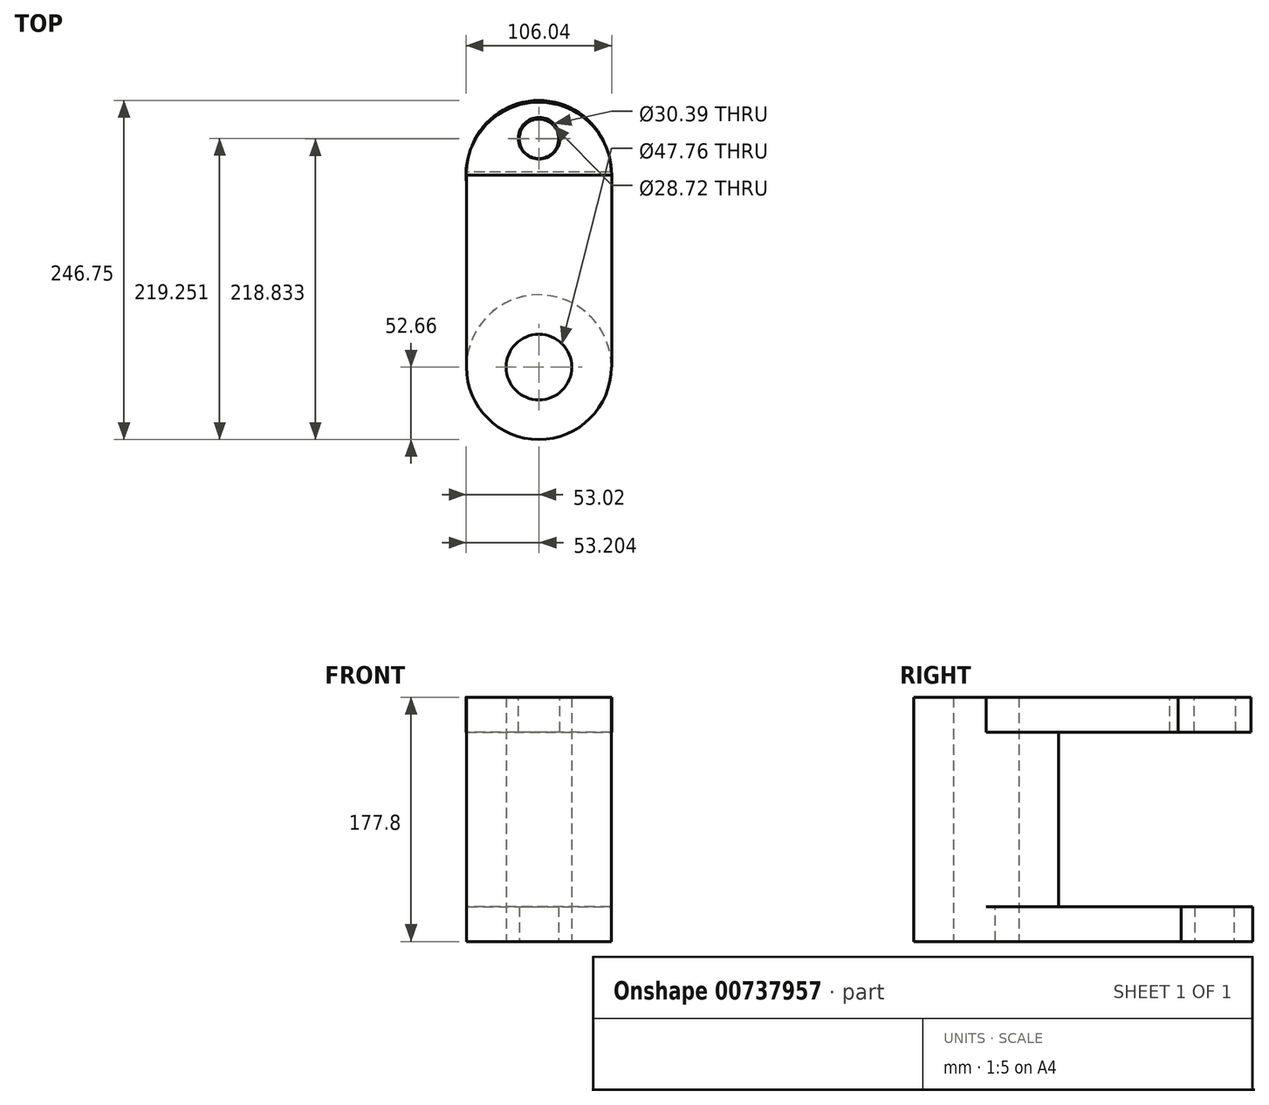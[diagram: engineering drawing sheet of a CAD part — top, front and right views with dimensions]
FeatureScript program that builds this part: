
annotation { "Feature Type Name" : "Feature", "Feature Type Description" : "" }
export const myFeature = defineFeature(function(context is Context, id is Id, definition is map)
    precondition{}
    {
        {
            var Q0;
            Q0=qCreatedBy(makeId("Top.planeOp"),FACE);
            var sketch = newSketch(context, id + "F0", { "sketchPlane" : qUnion([Q0])});
            skCircle(sketch, "E0", {"center": v(0, 0) * mm, "radius": 52.66 * mm});
            skCircle(sketch, "E1", {"center": v(0, 0) * mm, "radius": 23.88 * mm});
            skSolve(sketch);
        }
        {
            var Q0;
            Q0 = qSketchRegion(id + "F0", true);
            extrude(context, id + "F1", {"entities" : qUnion([Q0]), "depth" : 127 * mm, "offsetDistance" : 25.4 * mm});
        }
        {
            var Q0;
            Q0=makeQuery(id+"F1.opExtrude","CAP_FACE",FACE,{"disambiguationData":[OSD([sQuery(id+"F0.wireOp",EDGE,"E0"),sQuery(id+"F0.wireOp",EDGE,"E1")])],"isStart":false});
            var sketch = newSketch(context, id + "F2", { "sketchPlane" : qUnion([Q0])});
            skLineSegment(sketch, "E2.bottom", {"start": v(-52.66, 0) * mm, "end": v(53.02, 0) * mm});
            skLineSegment(sketch, "E2.top", {"start": v(-52.66, 76.3) * mm, "end": v(53.02, 76.3) * mm});
            skLineSegment(sketch, "E2.left", {"start": v(-52.66, 0) * mm, "end": v(-52.66, 76.3) * mm});
            skLineSegment(sketch, "E2.right", {"start": v(53.02, 0) * mm, "end": v(53.02, 76.3) * mm});
            skSolve(sketch);
        }
        {
            var Q0;
            {var subQ0=sQuery(id+"F2.wireOp",EDGE,"E2.bottom");var subQ1=makeQuery(id+"F1.opExtrude","CAP_EDGE",EDGE,{"disambiguationData":[OSD([sQuery(id+"F0.wireOp",EDGE,"E0")])],"isStart":false});var subQ6=makeQuery(id+"F2.imprint","INTERSECT",VERTEX,{"derivedFrom":[subQ1,subQ0]});Q0=makeQuery(id+"F2.imprint","IMPRINT",FACE,{"disambiguationData":[TD([[makeQuery(id+"F2.imprint","IMPRINT",EDGE,{"disambiguationData":[TD([[subQ6,1.0]])],"derivedFrom":subQ0}),1.0]])]});}
            var Q1;
            {var subQ0=sQuery(id+"F2.wireOp",EDGE,"E2.bottom");var subQ1=makeQuery(id+"F1.opExtrude","CAP_EDGE",EDGE,{"disambiguationData":[OSD([sQuery(id+"F0.wireOp",EDGE,"E1")])],"isStart":false});var subQ2=makeQuery(id+"F2.imprint","INTERSECT",VERTEX,{"disambiguationData":[OD(0.0)],"derivedFrom":[subQ1,subQ0]});Q1=makeQuery(id+"F2.imprint","IMPRINT",FACE,{"disambiguationData":[TD([[makeQuery(id+"F2.imprint","IMPRINT",EDGE,{"disambiguationData":[TD([[subQ2,-1.0]])],"derivedFrom":subQ0}),1.0]])]});}
            var Q2;
            Q2=makeQuery(id+"F2.imprint","IMPRINT",FACE,{"disambiguationData":[TD([[makeQuery(id+"F2.imprint","IMPRINT",EDGE,{"derivedFrom":sQuery(id+"F2.wireOp",EDGE,"E2.top")}),-1.0]])]});
            extrude(context, id + "F3", {"entities" : qUnion([Q0, Q1, Q2]), "operationType" : NewBodyOperationType.ADD, "depth" : 25.4 * mm, "offsetDistance" : 25.4 * mm});
        }
        {
            var Q0;
            Q0=makeQuery(id+"F1.opExtrude","CAP_FACE",FACE,{"disambiguationData":[OSD([sQuery(id+"F0.wireOp",EDGE,"E0"),sQuery(id+"F0.wireOp",EDGE,"E1")])],"isStart":true});
            var sketch = newSketch(context, id + "F4", { "sketchPlane" : qUnion([Q0])});
            skLineSegment(sketch, "E3.bottom", {"start": v(52.66, 0) * mm, "end": v(-52.2, 0) * mm});
            skLineSegment(sketch, "E3.top", {"start": v(52.66, -78.38) * mm, "end": v(-52.2, -78.38) * mm});
            skLineSegment(sketch, "E3.left", {"start": v(52.66, 0) * mm, "end": v(52.66, -78.38) * mm});
            skLineSegment(sketch, "E3.right", {"start": v(-52.2, 0) * mm, "end": v(-52.2, -78.38) * mm});
            skSolve(sketch);
        }
        {
            var Q0;
            {var subQ0=sQuery(id+"F4.wireOp",EDGE,"E3.bottom");var subQ3=sQuery(id+"F4.wireOp",EDGE,"E3.right");var subQ5=makeQuery(id+"F4.imprint","INTERSECT",VERTEX,{"derivedFrom":[subQ0,subQ3]});Q0=makeQuery(id+"F4.imprint","IMPRINT",FACE,{"disambiguationData":[TD([[makeQuery(id+"F4.imprint","IMPRINT",EDGE,{"disambiguationData":[TD([[subQ5,1.0]])],"derivedFrom":subQ0}),1.0]])]});}
            var Q1;
            {var subQ0=sQuery(id+"F4.wireOp",EDGE,"E3.bottom");var subQ1=makeQuery(id+"F1.opExtrude","CAP_EDGE",EDGE,{"disambiguationData":[OSD([sQuery(id+"F0.wireOp",EDGE,"E1")])],"isStart":true});var subQ2=makeQuery(id+"F4.imprint","INTERSECT",VERTEX,{"disambiguationData":[OD(0.0)],"derivedFrom":[subQ1,subQ0]});Q1=makeQuery(id+"F4.imprint","IMPRINT",FACE,{"disambiguationData":[TD([[makeQuery(id+"F4.imprint","IMPRINT",EDGE,{"disambiguationData":[TD([[subQ2,-1.0]])],"derivedFrom":subQ0}),1.0]])]});}
            var Q2;
            {var subQ0=sQuery(id+"F4.wireOp",EDGE,"E3.top");Q2=makeQuery(id+"F4.imprint","IMPRINT",FACE,{"disambiguationData":[TD([[makeQuery(id+"F4.imprint","IMPRINT",EDGE,{"derivedFrom":subQ0}),-1.0]])]});}
            extrude(context, id + "F5", {"entities" : qUnion([Q0, Q1, Q2]), "operationType" : NewBodyOperationType.ADD, "depth" : 25.4 * mm, "offsetDistance" : 25.4 * mm});
        }
        {
            var Q0;
            Q0=makeQuery(id+"F5.opExtrude","SWEPT_FACE",FACE,{"disambiguationData":[OSD([sQuery(id+"F4.wireOp",EDGE,"E3.top")])]});
            extrude(context, id + "F6", {"entities" : qUnion([Q0]), "operationType" : NewBodyOperationType.ADD, "depth" : 25.4 * mm, "offsetDistance" : 25.4 * mm});
        }
        {
            var Q0;
            Q0=makeQuery(id+"F3.opExtrude","SWEPT_FACE",FACE,{"disambiguationData":[OSD([sQuery(id+"F2.wireOp",EDGE,"E2.top")])]});
            extrude(context, id + "F7", {"entities" : qUnion([Q0]), "operationType" : NewBodyOperationType.ADD, "depth" : 25.4 * mm, "offsetDistance" : 25.4 * mm});
        }
        {
            var Q0;
            Q0=makeQuery(id+"F6.opExtrude","CAP_FACE",FACE,{"disambiguationData":[OSD([sQuery(id+"F4.wireOp",EDGE,"E3.top")])],"isStart":false});
            extrude(context, id + "F8", {"entities" : qUnion([Q0]), "operationType" : NewBodyOperationType.ADD, "depth" : 38.1 * mm, "offsetDistance" : 25.4 * mm});
        }
        {
            var Q0;
            Q0=makeQuery(id+"F7.opExtrude","CAP_FACE",FACE,{"disambiguationData":[OSD([sQuery(id+"F2.wireOp",EDGE,"E2.top")])],"isStart":false});
            extrude(context, id + "F9", {"entities" : qUnion([Q0]), "operationType" : NewBodyOperationType.ADD, "depth" : 38.1 * mm, "offsetDistance" : 25.4 * mm});
        }
        {
            var Q0;
            {var subQ0=sQuery(id+"F2.wireOp",EDGE,"E2.top");var subQ1=makeQuery(id+"F3.opExtrude","CAP_EDGE",EDGE,{"disambiguationData":[OSD([subQ0])],"isStart":false});Q0=makeQuery(id+"F9.boolean.opBoolean","MERGE",FACE,{"derivedFrom":[makeQuery(id+"F7.boolean.opBoolean","MERGE",FACE,{"derivedFrom":[makeQuery(id+"F3.opExtrude","CAP_FACE",FACE,{"disambiguationData":[OSD([sQuery(id+"F2.wireOp",EDGE,"E2.bottom"),subQ0,sQuery(id+"F2.wireOp",EDGE,"E2.left"),sQuery(id+"F2.wireOp",EDGE,"E2.right")])],"isStart":false}),makeQuery(id+"F7.opExtrude","SWEPT_FACE",FACE,{"disambiguationData":[OSD([subQ0]),TDD([subQ1])]})]}),makeQuery(id+"F9.opExtrude","SWEPT_FACE",FACE,{"disambiguationData":[OSD([subQ0]),TDD([makeQuery(id+"F7.opExtrude","CAP_EDGE",EDGE,{"disambiguationData":[OSD([subQ0]),TDD([subQ1])],"isStart":false})])]})]});}
            var sketch = newSketch(context, id + "F10", { "sketchPlane" : qUnion([Q0])});
            skCircle(sketch, "E4", {"center": v(0, 139.8) * mm, "radius": 53.02 * mm});
            skSolve(sketch);
        }
        {
            var Q0;
            {var subQ2=sQuery(id+"F2.wireOp",EDGE,"E2.top");var subQ4=makeQuery(id+"F9.opExtrude","CAP_EDGE",EDGE,{"disambiguationData":[OSD([subQ2]),TDD([makeQuery(id+"F7.opExtrude","CAP_EDGE",EDGE,{"disambiguationData":[OSD([subQ2]),TDD([makeQuery(id+"F3.opExtrude","CAP_EDGE",EDGE,{"disambiguationData":[OSD([subQ2])],"isStart":false})])],"isStart":false})])],"isStart":false});Q0=makeQuery(id+"F10.imprint","IMPRINT",FACE,{"disambiguationData":[TD([[makeQuery(id+"F10.imprint","IMPRINT",EDGE,{"derivedFrom":subQ4}),1.0]])]});}
            extrude(context, id + "F11", {"entities" : qUnion([Q0]), "oppositeDirection" : true, "depth" : 25.4 * mm, "offsetDistance" : 25.4 * mm});
        }
        {
            var Q0;
            {var subQ0=sQuery(id+"F4.wireOp",EDGE,"E3.top");var subQ1=makeQuery(id+"F5.opExtrude","CAP_EDGE",EDGE,{"disambiguationData":[OSD([subQ0])],"isStart":false});Q0=makeQuery(id+"F8.boolean.opBoolean","MERGE",FACE,{"derivedFrom":[makeQuery(id+"F6.boolean.opBoolean","MERGE",FACE,{"derivedFrom":[makeQuery(id+"F5.opExtrude","CAP_FACE",FACE,{"disambiguationData":[OSD([sQuery(id+"F4.wireOp",EDGE,"E3.bottom"),subQ0,sQuery(id+"F4.wireOp",EDGE,"E3.left"),sQuery(id+"F4.wireOp",EDGE,"E3.right")])],"isStart":false}),makeQuery(id+"F6.opExtrude","SWEPT_FACE",FACE,{"disambiguationData":[OSD([subQ0]),TDD([subQ1])]})]}),makeQuery(id+"F8.opExtrude","SWEPT_FACE",FACE,{"disambiguationData":[OSD([subQ0]),TDD([makeQuery(id+"F6.opExtrude","CAP_EDGE",EDGE,{"disambiguationData":[OSD([subQ0]),TDD([subQ1])],"isStart":false})])]})]});}
            var sketch = newSketch(context, id + "F12", { "sketchPlane" : qUnion([Q0])});
            skCircle(sketch, "E5", {"center": v(0, -141.88) * mm, "radius": 52.2 * mm});
            skSolve(sketch);
        }
        {
            var Q0;
            {var subQ0=sQuery(id+"F12.wireOp",EDGE,"E5");var subQ2=sQuery(id+"F4.wireOp",EDGE,"E3.top");var subQ4=makeQuery(id+"F8.opExtrude","CAP_EDGE",EDGE,{"disambiguationData":[OSD([subQ2]),TDD([makeQuery(id+"F6.opExtrude","CAP_EDGE",EDGE,{"disambiguationData":[OSD([subQ2]),TDD([makeQuery(id+"F5.opExtrude","CAP_EDGE",EDGE,{"disambiguationData":[OSD([subQ2])],"isStart":false})])],"isStart":false})])],"isStart":false});var subQ6=makeQuery(id+"F12.imprint","INTERSECT",VERTEX,{"derivedFrom":[subQ4,subQ0]});Q0=makeQuery(id+"F12.imprint","IMPRINT",FACE,{"disambiguationData":[TD([[makeQuery(id+"F12.imprint","IMPRINT",EDGE,{"disambiguationData":[TD([[subQ6,1.0]])],"derivedFrom":subQ0}),1.0]])]});}
            extrude(context, id + "F13", {"entities" : qUnion([Q0]), "oppositeDirection" : true, "depth" : 25.4 * mm, "offsetDistance" : 25.4 * mm});
        }
        {
            var Q0;
            Q0=makeQuery(id+"F1.opExtrude","CAP_FACE",FACE,{"disambiguationData":[OSD([sQuery(id+"F0.wireOp",EDGE,"E0"),sQuery(id+"F0.wireOp",EDGE,"E1")])],"isStart":true});
            extrude(context, id + "F14", {"entities" : qUnion([Q0]), "operationType" : NewBodyOperationType.ADD, "depth" : 25.4 * mm, "offsetDistance" : 25.4 * mm});
        }
        {
            var Q0;
            Q0=makeQuery(id+"F1.opExtrude","CAP_FACE",FACE,{"disambiguationData":[OSD([sQuery(id+"F0.wireOp",EDGE,"E0"),sQuery(id+"F0.wireOp",EDGE,"E1")])],"isStart":false});
            extrude(context, id + "F15", {"entities" : qUnion([Q0]), "operationType" : NewBodyOperationType.ADD, "depth" : 25.4 * mm, "offsetDistance" : 25.4 * mm});
        }
        {
            var Q0;
            {var subQ0=sQuery(id+"F2.wireOp",EDGE,"E2.top");var subQ1=makeQuery(id+"F3.opExtrude","CAP_EDGE",EDGE,{"disambiguationData":[OSD([subQ0])],"isStart":false});Q0=makeQuery(id+"F15.boolean.opBoolean","MERGE",FACE,{"derivedFrom":[makeQuery(id+"F9.boolean.opBoolean","MERGE",FACE,{"derivedFrom":[makeQuery(id+"F7.boolean.opBoolean","MERGE",FACE,{"derivedFrom":[makeQuery(id+"F3.opExtrude","CAP_FACE",FACE,{"disambiguationData":[OSD([sQuery(id+"F2.wireOp",EDGE,"E2.bottom"),subQ0,sQuery(id+"F2.wireOp",EDGE,"E2.left"),sQuery(id+"F2.wireOp",EDGE,"E2.right")])],"isStart":false}),makeQuery(id+"F7.opExtrude","SWEPT_FACE",FACE,{"disambiguationData":[OSD([subQ0]),TDD([subQ1])]})]}),makeQuery(id+"F9.opExtrude","SWEPT_FACE",FACE,{"disambiguationData":[OSD([subQ0]),TDD([makeQuery(id+"F7.opExtrude","CAP_EDGE",EDGE,{"disambiguationData":[OSD([subQ0]),TDD([subQ1])],"isStart":false})])]})]}),makeQuery(id+"F15.opExtrude","CAP_FACE",FACE,{"disambiguationData":[OSD([sQuery(id+"F0.wireOp",EDGE,"E0"),sQuery(id+"F0.wireOp",EDGE,"E1")])],"isStart":false})]});}
            var sketch = newSketch(context, id + "F16", { "sketchPlane" : qUnion([Q0])});
            skCircle(sketch, "E6", {"center": v(0, 0) * mm, "radius": 23.88 * mm});
            skSolve(sketch);
        }
        {
            var Q0;
            {var subQ3=sQuery(id+"F2.wireOp",EDGE,"E2.bottom");var subQ4=sQuery(id+"F0.wireOp",EDGE,"E1");var subQ5=makeQuery(id+"F15.boolean.opBoolean","SPLIT",EDGE,{"disambiguationData":[TD([makeQuery(id+"F1.opExtrude","SWEPT_FACE",FACE,{"disambiguationData":[OSD([subQ4])]})])],"derivedFrom":makeQuery(id+"F3.opExtrude","CAP_EDGE",EDGE,{"disambiguationData":[OSD([subQ3])],"isStart":false})});Q0=makeQuery(id+"F16.imprint","IMPRINT",FACE,{"disambiguationData":[TD([[makeQuery(id+"F16.imprint","IMPRINT",EDGE,{"derivedFrom":subQ5}),1.0]])]});}
            extrude(context, id + "F17", {"entities" : qUnion([Q0]), "operationType" : NewBodyOperationType.REMOVE, "oppositeDirection" : true, "depth" : 228.6 * mm, "offsetDistance" : 25.4 * mm});
        }
        {
            var Q0;
            Q0=makeQuery(id+"F11.opExtrude","CAP_FACE",FACE,{"disambiguationData":[OSD([sQuery(id+"F2.wireOp",EDGE,"E2.top"),sQuery(id+"F2.wireOp",EDGE,"E2.left"),sQuery(id+"F10.wireOp",EDGE,"E4")])],"isStart":true});
            var sketch = newSketch(context, id + "F18", { "sketchPlane" : qUnion([Q0])});
            skCircle(sketch, "E7", {"center": v(0.18, 166.6) * mm, "radius": 15.2 * mm});
            skPoint(sketch, "E7.centerSnap0", {"position": v(0.18, 139.8) * mm});
            skSolve(sketch);
        }
        {
            var Q0;
            Q0 = qSketchRegion(id + "F18", true);
            extrude(context, id + "F19", {"entities" : qUnion([Q0]), "operationType" : NewBodyOperationType.REMOVE, "oppositeDirection" : true, "depth" : 25.4 * mm, "offsetDistance" : 25.4 * mm});
        }
        {
            var Q0;
            Q0=makeQuery(id+"F13.opExtrude","CAP_FACE",FACE,{"disambiguationData":[OSD([sQuery(id+"F4.wireOp",EDGE,"E3.top"),sQuery(id+"F12.wireOp",EDGE,"E5")])],"isStart":true});
            var sketch = newSketch(context, id + "F20", { "sketchPlane" : qUnion([Q0])});
            skCircle(sketch, "E8", {"center": v(0, -166.17) * mm, "radius": 14.36 * mm});
            skPoint(sketch, "E8.centerSnap0", {"position": v(0, -141.88) * mm});
            skSolve(sketch);
        }
        {
            var Q0;
            Q0 = qSketchRegion(id + "F20", true);
            extrude(context, id + "F21", {"entities" : qUnion([Q0]), "operationType" : NewBodyOperationType.REMOVE, "oppositeDirection" : true, "depth" : 25.4 * mm, "offsetDistance" : 25.4 * mm});
        }
    });
